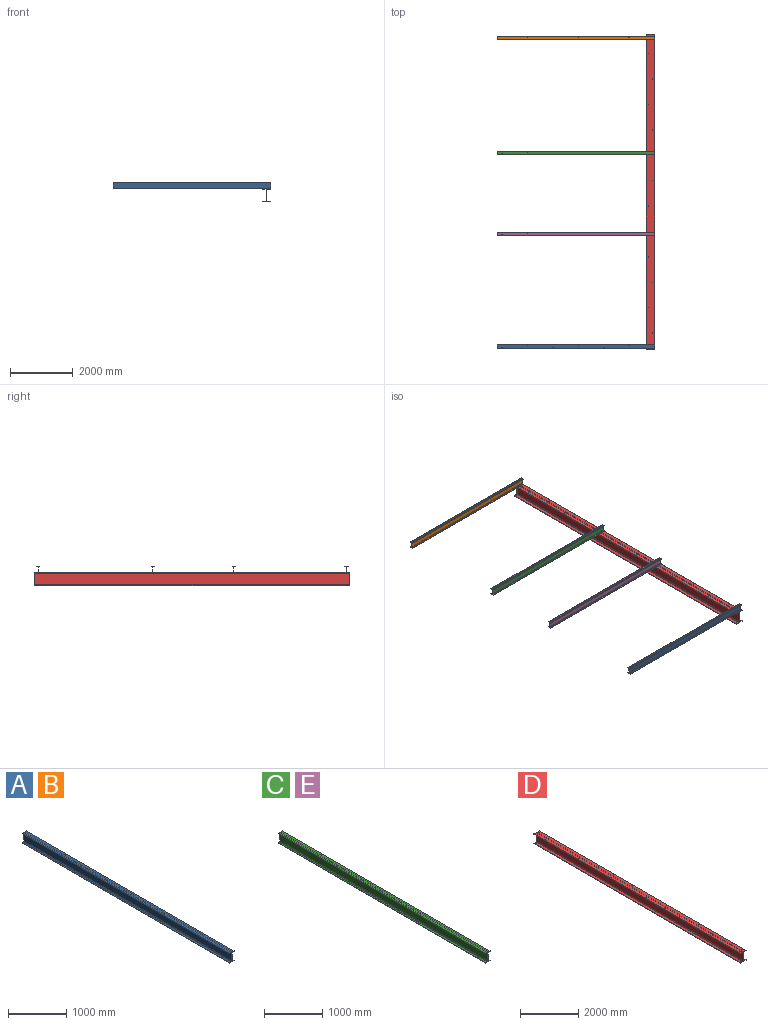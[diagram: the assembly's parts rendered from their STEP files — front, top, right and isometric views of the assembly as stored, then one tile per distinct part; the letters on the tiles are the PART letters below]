
ASSEMBLY  parts=5 mates=4
PART A: 28 faces, bbox 101.6x5029.2x202.9 mm
  f0: plane 5029.2x35.18mm, normal (0,0,1), area 176348.2mm2, adj f4,f5,f16,f17,f26,f27
  f1: plane 5029.2x101.6mm, normal (0,0,-1), area 509818.7mm2, adj f5,f6,f16,f17,f24,f25,f26,f27
  f2: cylinder r=12.7mm len=5029.2mm, axis (0,1,0), area 100328.1mm2, adj f3,f15,f16,f17
  f3: plane 5029.2x164.59mm, normal (-1,0,0), area 827766.1mm2, adj f2,f4,f16,f17
  f4: cylinder r=12.7mm len=5029.2mm, axis (0,1,0), area 100328.1mm2, adj f0,f3,f16,f17
  f5: plane 5029.2x6.48mm, normal (-1,0,0), area 32574.1mm2, adj f0,f1,f16,f17
  f6: plane 5029.2x6.48mm, normal (1,0,0), area 32574.1mm2, adj f1,f7,f16,f17
  f7: plane 5029.2x35.18mm, normal (0,0,1), area 176348.2mm2, adj f6,f8,f16,f17,f24,f25
  f8: cylinder r=12.7mm len=5029.2mm, axis (0,1,0), area 100328.1mm2, adj f7,f9,f16,f17
  f9: plane 5029.2x164.59mm, normal (1,0,0), area 827766.1mm2, adj f8,f10,f16,f17
  f10: cylinder r=12.7mm len=5029.2mm, axis (0,1,0), area 100328.1mm2, adj f9,f11,f16,f17
  f11: plane 5029.2x35.18mm, normal (0,0,-1), area 176441.3mm2, adj f10,f12,f16,f17,f21,f22,f23
  f12: plane 5029.2x6.48mm, normal (1,0,0), area 32574.1mm2, adj f11,f13,f16,f17
  f13: plane 5029.2x101.6mm, normal (0,0,1), area 510004.8mm2, adj f12,f14,f16,f17,f18,f19,f20,f21
  f14: plane 5029.2x6.48mm, normal (-1,0,0), area 32574.1mm2, adj f13,f15,f16,f17
  f15: plane 5029.2x35.18mm, normal (0,0,-1), area 176441.3mm2, adj f2,f14,f16,f17,f18,f19,f20
  f16: plane 202.95x101.6mm, normal (0,-1,0), area 2564.5mm2, adj f0,f1,f2,f3,f4,f5,f6,f7
  f17: plane 202.95x101.6mm, normal (0,1,0), area 2564.5mm2, adj f0,f1,f2,f3,f4,f5,f6,f7
  f18: cylinder r=7.14mm len=14.29mm, axis (0,0,1), area 290.7mm2, adj f13,f15
  f19: cylinder r=7.14mm len=14.29mm, axis (0,0,1), area 290.7mm2, adj f13,f15
  f20: cylinder r=7.14mm len=14.29mm, axis (0,0,1), area 290.7mm2, adj f13,f15
  f21: cylinder r=7.14mm len=14.29mm, axis (0,0,1), area 290.7mm2, adj f11,f13
  f22: cylinder r=7.14mm len=14.29mm, axis (0,0,1), area 290.7mm2, adj f11,f13
  f23: cylinder r=7.14mm len=14.29mm, axis (0,0,1), area 290.7mm2, adj f11,f13
  f24: cylinder r=10.32mm len=20.64mm, axis (0,0,-1), area 419.9mm2, adj f1,f7
  f25: cylinder r=8.73mm len=17.46mm, axis (0,0,-1), area 355.3mm2, adj f1,f7
  f26: cylinder r=8.73mm len=17.46mm, axis (0,0,-1), area 355.3mm2, adj f0,f1
  f27: cylinder r=10.32mm len=20.64mm, axis (0,0,-1), area 419.9mm2, adj f0,f1
PART B: same geometry as A
PART C: 24 faces, bbox 101.6x5029.2x202.9 mm
  f0: plane 5029.2x35.18mm, normal (0,0,1), area 176348.2mm2, adj f4,f5,f16,f17,f22,f23
  f1: plane 5029.2x101.6mm, normal (0,0,-1), area 509818.7mm2, adj f5,f6,f16,f17,f20,f21,f22,f23
  f2: cylinder r=12.7mm len=5029.2mm, axis (0,1,0), area 100328.1mm2, adj f3,f15,f16,f17
  f3: plane 5029.2x164.59mm, normal (-1,0,0), area 827766.1mm2, adj f2,f4,f16,f17
  f4: cylinder r=12.7mm len=5029.2mm, axis (0,1,0), area 100328.1mm2, adj f0,f3,f16,f17
  f5: plane 5029.2x6.48mm, normal (-1,0,0), area 32574.1mm2, adj f0,f1,f16,f17
  f6: plane 5029.2x6.48mm, normal (1,0,0), area 32574.1mm2, adj f1,f7,f16,f17
  f7: plane 5029.2x35.18mm, normal (0,0,1), area 176348.2mm2, adj f6,f8,f16,f17,f20,f21
  f8: cylinder r=12.7mm len=5029.2mm, axis (0,1,0), area 100328.1mm2, adj f7,f9,f16,f17
  f9: plane 5029.2x164.59mm, normal (1,0,0), area 827766.1mm2, adj f8,f10,f16,f17
  f10: cylinder r=12.7mm len=5029.2mm, axis (0,1,0), area 100328.1mm2, adj f9,f11,f16,f17
  f11: plane 5029.2x35.18mm, normal (0,0,-1), area 176761.9mm2, adj f10,f12,f16,f17,f19
  f12: plane 5029.2x6.48mm, normal (1,0,0), area 32574.1mm2, adj f11,f13,f16,f17
  f13: plane 5029.2x101.6mm, normal (0,0,1), area 510646.1mm2, adj f12,f14,f16,f17,f18,f19
  f14: plane 5029.2x6.48mm, normal (-1,0,0), area 32574.1mm2, adj f13,f15,f16,f17
  f15: plane 5029.2x35.18mm, normal (0,0,-1), area 176761.9mm2, adj f2,f14,f16,f17,f18
  f16: plane 202.95x101.6mm, normal (0,-1,0), area 2564.5mm2, adj f0,f1,f2,f3,f4,f5,f6,f7
  f17: plane 202.95x101.6mm, normal (0,1,0), area 2564.5mm2, adj f0,f1,f2,f3,f4,f5,f6,f7
  f18: cylinder r=7.14mm len=14.29mm, axis (0,0,1), area 290.7mm2, adj f13,f15
  f19: cylinder r=7.14mm len=14.29mm, axis (0,0,1), area 290.7mm2, adj f11,f13
  f20: cylinder r=10.32mm len=20.64mm, axis (0,0,-1), area 419.9mm2, adj f1,f7
  f21: cylinder r=8.73mm len=17.46mm, axis (0,0,-1), area 355.3mm2, adj f1,f7
  f22: cylinder r=8.73mm len=17.46mm, axis (0,0,-1), area 355.3mm2, adj f0,f1
  f23: cylinder r=10.32mm len=20.64mm, axis (0,0,-1), area 419.9mm2, adj f0,f1
PART D: 40 faces, bbox 260x10045.7x414.8 mm
  f0: plane 10045.7x259.97mm, normal (0,0,-1), area 2610612.6mm2, adj f5,f6,f16,f17,f36,f37,f38,f39
  f1: cylinder r=12.7mm len=10045.7mm, axis (0,1,0), area 200402.8mm2, adj f2,f15,f16,f17
  f2: plane 10045.7x355.6mm, normal (-1,0,0), area 3572250.9mm2, adj f1,f3,f16,f17
  f3: cylinder r=12.7mm len=10045.7mm, axis (0,1,0), area 200402.8mm2, adj f2,f4,f16,f17
  f4: plane 10045.7x112.27mm, normal (0,0,1), area 1127331.7mm2, adj f3,f5,f16,f17,f38,f39
  f5: plane 10045.7x16.89mm, normal (-1,0,0), area 169681.9mm2, adj f0,f4,f16,f17
  f6: plane 10045.7x16.89mm, normal (1,0,0), area 169681.9mm2, adj f0,f7,f16,f17
  f7: plane 10045.7x112.27mm, normal (0,0,1), area 1127331.7mm2, adj f6,f8,f16,f17,f36,f37
  f8: cylinder r=12.7mm len=10045.7mm, axis (0,1,0), area 200402.8mm2, adj f7,f9,f16,f17
  f9: plane 10045.7x355.6mm, normal (1,0,0), area 3572250.9mm2, adj f8,f10,f16,f17
  f10: cylinder r=12.7mm len=10045.7mm, axis (0,1,0), area 200402.8mm2, adj f9,f11,f16,f17
  f11: plane 10045.7x112.27mm, normal (0,0,-1), area 1126051mm2, adj f10,f12,f16,f17,f27,f28,f29,f30
  f12: plane 10045.7x16.89mm, normal (1,0,0), area 169681.9mm2, adj f11,f13,f16,f17
  f13: plane 10045.7x259.97mm, normal (0,0,1), area 2608051.3mm2, adj f12,f14,f16,f17,f18,f19,f20,f21
  f14: plane 10045.7x16.89mm, normal (-1,0,0), area 169681.9mm2, adj f13,f15,f16,f17
  f15: plane 10045.7x112.27mm, normal (0,0,-1), area 1126051mm2, adj f1,f14,f16,f17,f18,f19,f20,f21
  f16: plane 414.78x259.97mm, normal (0,-1,0), area 12743.3mm2, adj f0,f1,f2,f3,f4,f5,f6,f7
  f17: plane 414.78x259.97mm, normal (0,1,0), area 12743.3mm2, adj f0,f1,f2,f3,f4,f5,f6,f7
  f18: cylinder r=7.14mm len=16.89mm, axis (0,0,1), area 758.2mm2, adj f13,f15
  f19: cylinder r=7.14mm len=16.89mm, axis (0,0,1), area 758.2mm2, adj f13,f15
  f20: cylinder r=7.14mm len=16.89mm, axis (0,0,1), area 758.2mm2, adj f13,f15
  f21: cylinder r=7.14mm len=16.89mm, axis (0,0,1), area 758.2mm2, adj f13,f15
  f22: cylinder r=7.14mm len=16.89mm, axis (0,0,1), area 758.2mm2, adj f13,f15
  f23: cylinder r=8.73mm len=17.46mm, axis (0,0,1), area 926.6mm2, adj f13,f15
  f24: cylinder r=8.73mm len=17.46mm, axis (0,0,1), area 926.6mm2, adj f13,f15
  f25: cylinder r=8.73mm len=17.46mm, axis (0,0,1), area 926.6mm2, adj f13,f15
  f26: cylinder r=8.73mm len=17.46mm, axis (0,0,1), area 926.6mm2, adj f13,f15
  f27: cylinder r=7.14mm len=16.89mm, axis (0,0,1), area 758.2mm2, adj f11,f13
  f28: cylinder r=7.14mm len=16.89mm, axis (0,0,1), area 758.2mm2, adj f11,f13
  f29: cylinder r=7.14mm len=16.89mm, axis (0,0,1), area 758.2mm2, adj f11,f13
  f30: cylinder r=7.14mm len=16.89mm, axis (0,0,1), area 758.2mm2, adj f11,f13
  f31: cylinder r=7.14mm len=16.89mm, axis (0,0,1), area 758.2mm2, adj f11,f13
  f32: cylinder r=8.73mm len=17.46mm, axis (0,0,1), area 926.6mm2, adj f11,f13
  f33: cylinder r=8.73mm len=17.46mm, axis (0,0,1), area 926.6mm2, adj f11,f13
  f34: cylinder r=8.73mm len=17.46mm, axis (0,0,1), area 926.6mm2, adj f11,f13
  f35: cylinder r=8.73mm len=17.46mm, axis (0,0,1), area 926.6mm2, adj f11,f13
  f36: cylinder r=8.73mm len=17.46mm, axis (0,0,-1), area 926.6mm2, adj f0,f7
  f37: cylinder r=8.73mm len=17.46mm, axis (0,0,-1), area 926.6mm2, adj f0,f7
  f38: cylinder r=8.73mm len=17.46mm, axis (0,0,-1), area 926.6mm2, adj f0,f4
  f39: cylinder r=8.73mm len=17.46mm, axis (0,0,-1), area 926.6mm2, adj f0,f4
PART E: same geometry as C
PLACE A rot(axis=(0,0,1),90deg) t=(-4954.91,-5700.65,-13.88)mm
PLACE B rot(axis=(0,0,1),90deg) t=(-4954.91,4154.29,-14.44)mm
PLACE C rot(axis=(0,0,1),90deg) t=(-4954.91,493.51,-14.41)mm
PLACE D rot(axis=(0,0,1),180deg) t=(-56.07,-5780.29,-323.63)mm
PLACE E rot(axis=(0,0,1),90deg) t=(-4954.91,-2097.29,-14.2)mm
MATE cylindrical D.f23 <-> A.f25  axis (0,0,1) through (13.97,-5672.08,-124.69)mm
MATE cylindrical D.f26 <-> B.f25  axis (0,0,1) through (13.97,4182.86,-124.69)mm
MATE cylindrical D.f25 <-> C.f21  axis (0,0,1) through (13.97,522.09,-116.24)mm
MATE cylindrical D.f24 <-> E.f21  axis (0,0,1) through (13.97,-2068.71,-124.69)mm
